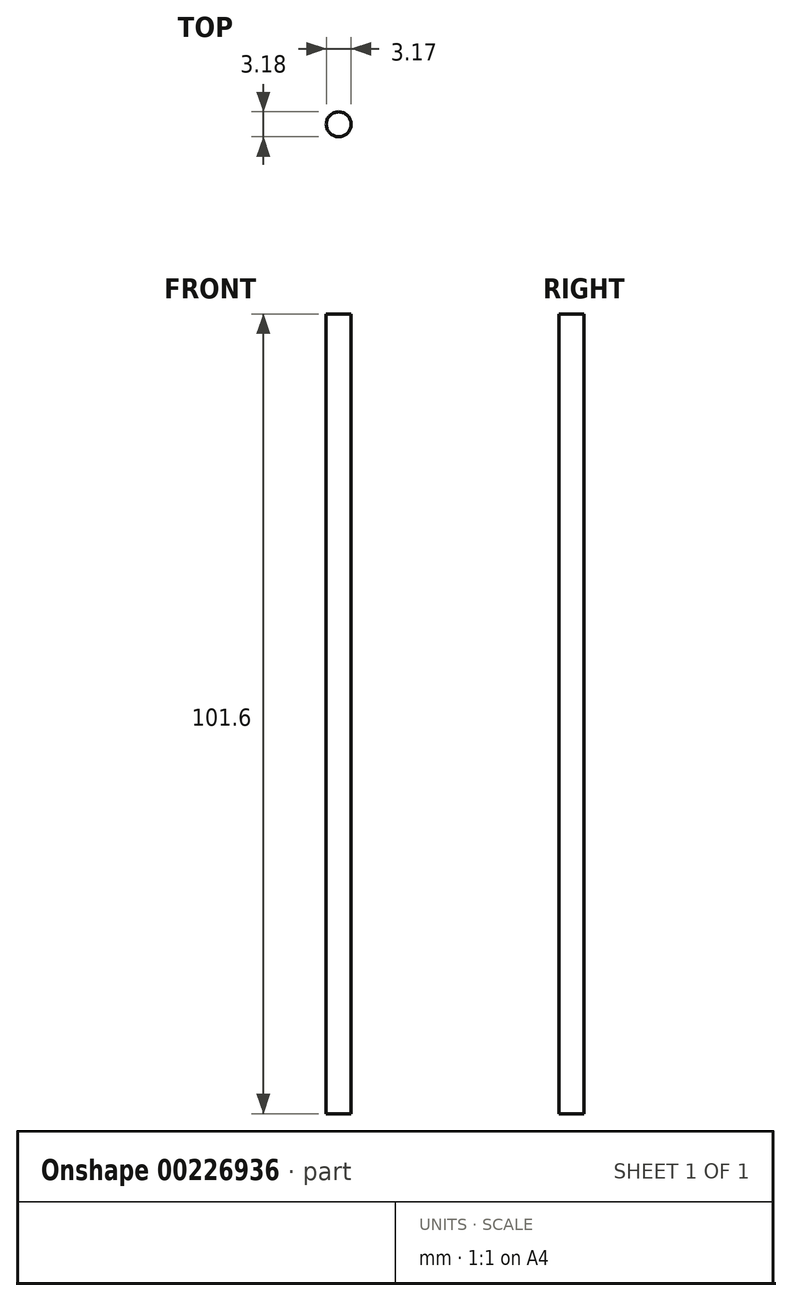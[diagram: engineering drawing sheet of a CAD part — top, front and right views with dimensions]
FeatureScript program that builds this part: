
annotation { "Feature Type Name" : "Feature", "Feature Type Description" : "" }
export const myFeature = defineFeature(function(context is Context, id is Id, definition is map)
    precondition{}
    {
        {
            var Q0;
            Q0=qCreatedBy(makeId("Top.planeOp"),FACE);
            var sketch = newSketch(context, id + "F0", { "sketchPlane" : qUnion([Q0])});
            skCircle(sketch, "E0", {"center": v(-42.7, 30.87) * mm, "radius": 1.59 * mm});
            skSolve(sketch);
        }
        {
            var Q0;
            Q0=makeQuery(id+"F0.imprint","IMPRINT",FACE,{"disambiguationData":[TD([[makeQuery(id+"F0.imprint","IMPRINT",EDGE,{"derivedFrom":sQuery(id+"F0.wireOp",EDGE,"E0")}),1.0]])]});
            extrude(context, id + "F1", {"entities" : qUnion([Q0]), "depth" : 101.6 * mm});
        }
    });
